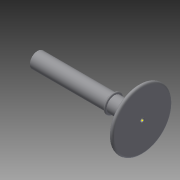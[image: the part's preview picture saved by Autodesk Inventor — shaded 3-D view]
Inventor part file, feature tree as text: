
AUTODESK INVENTOR PART (.ipt)
format: ipt  version: 2015 (Build 190159000, 159)  size: 149,504 bytes
history: native  units: mm
features: sketch x10, extrude x7, fillet x4, plane x3, revolve x1
ambient origin geometry x8: Origin, YZ Plane, XZ Plane, XY Plane, X Axis, Y Axis, Z Axis, Center Point
bodies: Solid1 (feature_tree)
feature tree (25):
  revolve  "Revolution1"  [1 undecoded]
  extrude  "Extrusion1"  Depth=4.1mm
  fillet  "Fillet1"  Radius=4.1mm
  plane  "Work Plane1"
  extrude  "Extrusion2"  Depth=8.0mm
  fillet  "Fillet2"  Radius=8.0mm
  plane  "Work Plane2"
  extrude  "Extrusion3"  [1 undecoded]
  plane  "Work Plane3"
  sketch  "Sketch5"  dims[d11=10.0mm d12=1.0mm d13=0.0mm]
  extrude  "Extrusion4"  Depth=1.0mm TaperAngle=0.0deg
  extrude  "Extrusion5"  [1 undecoded]
  sketch  "Sketch8"  dims[d19=8.0mm d20=0.0mm d21=4.0mm d22=0.0mm d28=7.4mm d29=47.0mm d30=0.0mm]
  extrude  "Extrusion7"  TaperAngle=0.0deg  [1 undecoded]
  extrude  "Extrusion8"  Depth=47.0mm TaperAngle=0.0deg
  fillet  "Fillet3"  Radius=7.4mm
  fillet  "Fillet4"  Radius=47.0mm
  sketch  "Sketch1"  dims[d0=50.0mm d1=16.0mm]
  sketch  "Sketch2"  dims[d2=2.0mm d3=4.1mm d4=4.1mm]
  sketch  "Sketch3"  dims[d5=90.0deg d6=1.75mm d7=8.0mm d8=0.0mm]
  sketch  "Sketch4"  dims[d9=0.3mm d10=-15.0mm]
  sketch  "Sketch6"  dims[d14=0.5mm d15=-1.0mm]
  sketch  "Sketch7"  dims[d16=10.0mm d17=0.0mm d18=0.0mm]
  sketch  "Sketch9"  dims[d31=2.5mm]
  sketch  "Sketch10"  dims[d32=8.0mm d33=0.0mm d34=0.5mm d35=1.0mm]
note: 4 required parameter values undecoded (feature->parameter linkage not recoverable at this tier; creation-order binding heuristic only, values carry confidence <= 0.55)